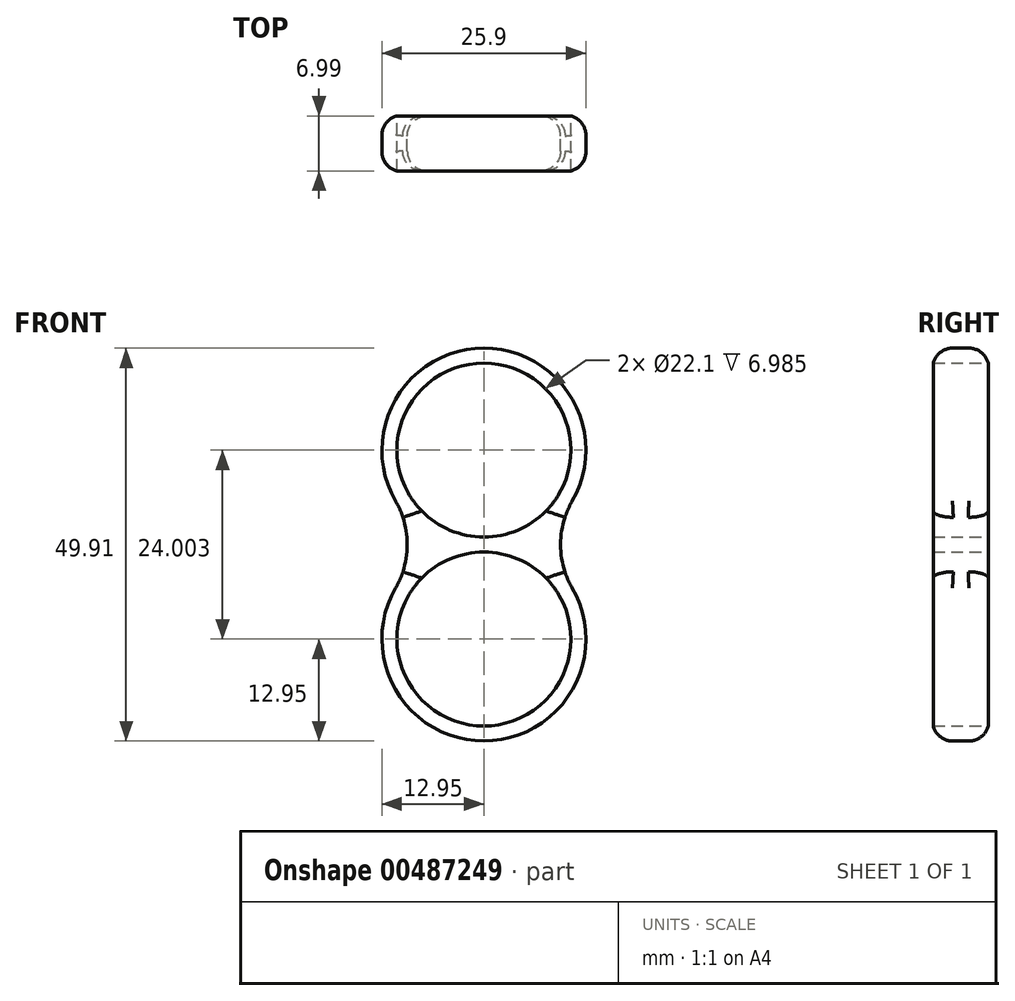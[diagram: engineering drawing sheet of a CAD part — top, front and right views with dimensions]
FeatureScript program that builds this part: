
annotation { "Feature Type Name" : "Feature", "Feature Type Description" : "" }
export const myFeature = defineFeature(function(context is Context, id is Id, definition is map)
    precondition{}
    {
        {
            var Q0;
            Q0=qCreatedBy(makeId("Front.planeOp"),FACE);
            var sketch = newSketch(context, id + "F0", { "sketchPlane" : qUnion([Q0])});
            skCircle(sketch, "E0", {"center": v(0, 0) * mm, "radius": 11.05 * mm});
            skCircle(sketch, "E1", {"center": v(0, 0) * mm, "radius": 12.95 * mm});
            skCircle(sketch, "E2", {"center": v(0, 24) * mm, "radius": 11.05 * mm});
            skCircle(sketch, "E3", {"center": v(0, 24) * mm, "radius": 12.95 * mm});
            skLineSegment(sketch, "E4", {"start": v(4.88, 12) * mm, "end": v(22.08, 12) * mm});
            skCircle(sketch, "E5", {"center": v(20.79, 12) * mm, "radius": 11.05 * mm});
            skLineSegment(sketch, "E6", {"start": v(0, 24) * mm, "end": v(0, 19.95) * mm});
            skCircle(sketch, "E7.MirrorC", {"center": v(-20.79, 12) * mm, "radius": 11.05 * mm});
            skSolve(sketch);
        }
        {
            var Q0;
            {var subQ6=sQuery(id+"F0.wireOp",EDGE,"E0");Q0=makeQuery(id+"F0.imprint","IMPRINT",FACE,{"disambiguationData":[TD([[makeQuery(id+"F0.imprint","IMPRINT",EDGE,{"derivedFrom":subQ6}),-1.0]])]});}
            var Q1;
            {var subQ0=sQuery(id+"F0.wireOp",EDGE,"E7.MirrorC");var subQ1=sQuery(id+"F0.wireOp",EDGE,"E1");var subQ2=makeQuery(id+"F0.imprint","INTERSECT",VERTEX,{"derivedFrom":[subQ1,subQ0]});Q1=makeQuery(id+"F0.imprint","IMPRINT",FACE,{"disambiguationData":[TD([[makeQuery(id+"F0.imprint","IMPRINT",EDGE,{"disambiguationData":[TD([[subQ2,1.0]])],"derivedFrom":subQ1}),-1.0]])]});}
            var Q2;
            {var subQ0=sQuery(id+"F0.wireOp",EDGE,"E2");Q2=makeQuery(id+"F0.imprint","IMPRINT",FACE,{"disambiguationData":[TD([[makeQuery(id+"F0.imprint","IMPRINT",EDGE,{"derivedFrom":subQ0}),-1.0]])]});}
            var Q3;
            {var subQ1=sQuery(id+"F0.wireOp",EDGE,"E1");var subQ3=makeQuery(id+"F0.imprint","INTERSECT",VERTEX,{"derivedFrom":[subQ1,sQuery(id+"F0.wireOp",EDGE,"E2")]});Q3=makeQuery(id+"F0.imprint","IMPRINT",FACE,{"disambiguationData":[TD([[makeQuery(id+"F0.imprint","IMPRINT",EDGE,{"disambiguationData":[TD([[subQ3,-1.0]])],"derivedFrom":subQ1}),1.0]])]});}
            var Q4;
            {var subQ1=sQuery(id+"F0.wireOp",EDGE,"E1");var subQ3=sQuery(id+"F0.wireOp",EDGE,"E5");var subQ4=makeQuery(id+"F0.imprint","INTERSECT",VERTEX,{"derivedFrom":[subQ1,subQ3]});Q4=makeQuery(id+"F0.imprint","IMPRINT",FACE,{"disambiguationData":[TD([[makeQuery(id+"F0.imprint","IMPRINT",EDGE,{"disambiguationData":[TD([[subQ4,1.0]])],"derivedFrom":subQ3}),-1.0]])]});}
            var Q5;
            {var subQ1=sQuery(id+"F0.wireOp",EDGE,"E3");var subQ3=sQuery(id+"F0.wireOp",EDGE,"E5");var subQ4=makeQuery(id+"F0.imprint","INTERSECT",VERTEX,{"derivedFrom":[subQ1,subQ3]});Q5=makeQuery(id+"F0.imprint","IMPRINT",FACE,{"disambiguationData":[TD([[makeQuery(id+"F0.imprint","IMPRINT",EDGE,{"disambiguationData":[TD([[subQ4,-1.0]])],"derivedFrom":subQ3}),-1.0]])]});}
            extrude(context, id + "F1", {"entities" : qUnion([Q0, Q1, Q2, Q3, Q4, Q5]), "depth" : 7 * mm});
        }
        {
            var Q0;
            Q0=makeQuery(id+"F1.opExtrude","CAP_EDGE",EDGE,{"disambiguationData":[OSD([sQuery(id+"F0.wireOp",EDGE,"E3")])],"isStart":false});
            var Q1;
            Q1=makeQuery(id+"F1.opExtrude","CAP_EDGE",EDGE,{"disambiguationData":[OSD([sQuery(id+"F0.wireOp",EDGE,"E5")])],"isStart":false});
            var Q2;
            Q2=makeQuery(id+"F1.opExtrude","CAP_EDGE",EDGE,{"disambiguationData":[OSD([sQuery(id+"F0.wireOp",EDGE,"E1")])],"isStart":false});
            var Q3;
            Q3=makeQuery(id+"F1.opExtrude","CAP_EDGE",EDGE,{"disambiguationData":[OSD([sQuery(id+"F0.wireOp",EDGE,"E7.MirrorC")])],"isStart":false});
            var Q4;
            Q4=makeQuery(id+"F1.opExtrude","CAP_EDGE",EDGE,{"disambiguationData":[OSD([sQuery(id+"F0.wireOp",EDGE,"E3")])],"isStart":true});
            var Q5;
            Q5=makeQuery(id+"F1.opExtrude","CAP_EDGE",EDGE,{"disambiguationData":[OSD([sQuery(id+"F0.wireOp",EDGE,"E5")])],"isStart":true});
            var Q6;
            Q6=makeQuery(id+"F1.opExtrude","CAP_EDGE",EDGE,{"disambiguationData":[OSD([sQuery(id+"F0.wireOp",EDGE,"E1")])],"isStart":true});
            var Q7;
            Q7=makeQuery(id+"F1.opExtrude","CAP_EDGE",EDGE,{"disambiguationData":[OSD([sQuery(id+"F0.wireOp",EDGE,"E7.MirrorC")])],"isStart":true});
            fillet(context, id + "F2", {"entities" : qUnion([Q0, Q1, Q2, Q3, Q4, Q5, Q6, Q7]), "radius" : 2.54 * mm, "tangentPropagation" : true, "allowEdgeOverflow" : false});
        }
    });
